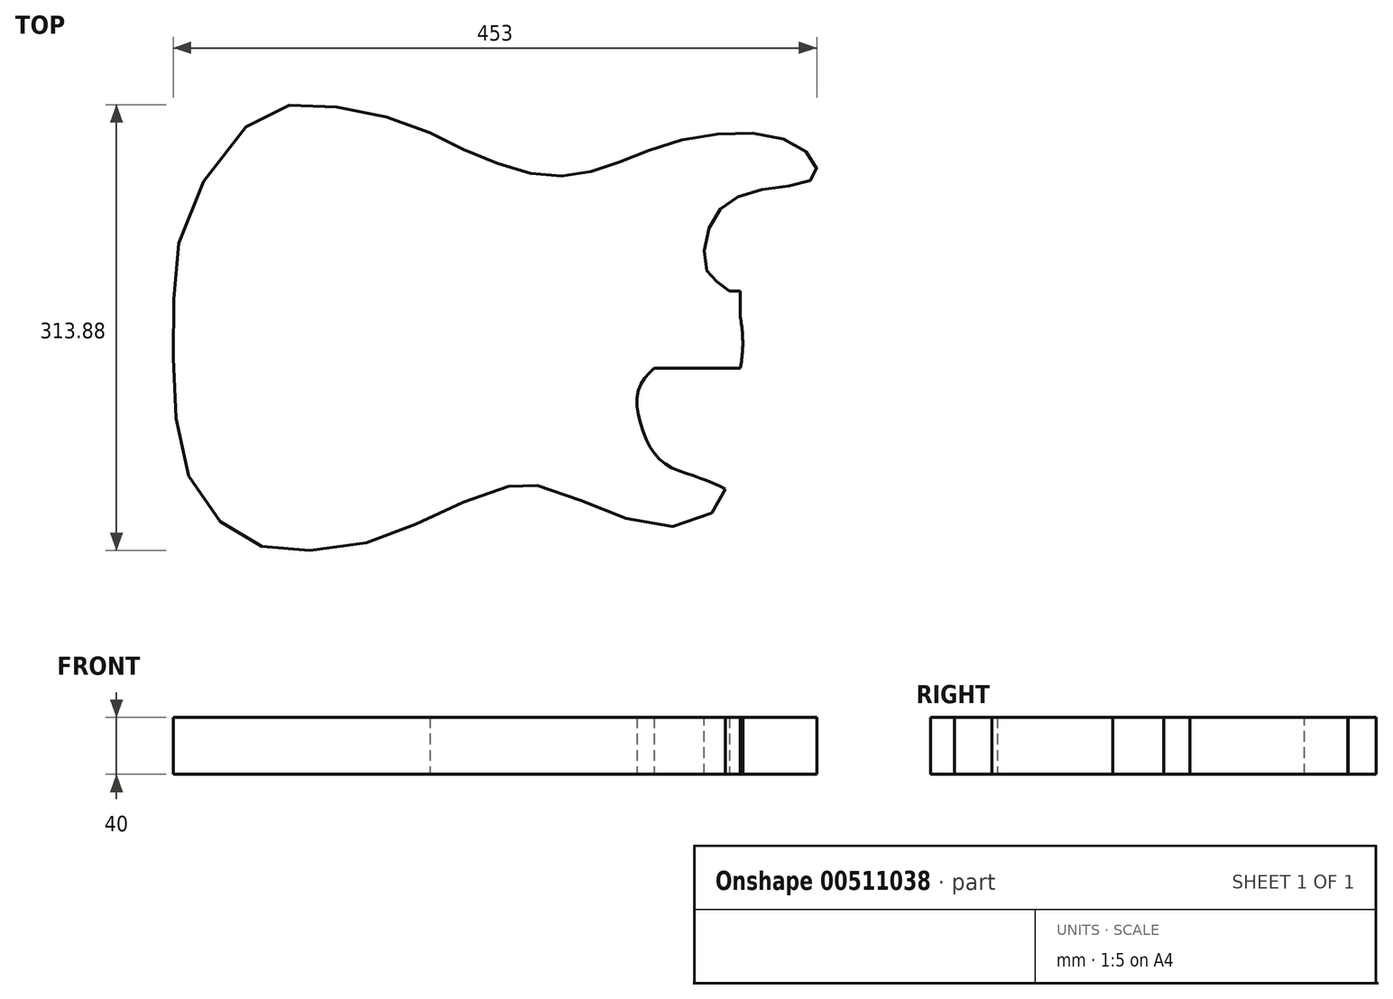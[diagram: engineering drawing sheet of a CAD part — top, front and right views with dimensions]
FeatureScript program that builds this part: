
annotation { "Feature Type Name" : "Feature", "Feature Type Description" : "" }
export const myFeature = defineFeature(function(context is Context, id is Id, definition is map)
    precondition{}
    {
        {
            var Q0;
            Q0=qCreatedBy(makeId("Top.planeOp"),FACE);
            var sketch = newSketch(context, id + "F0", { "sketchPlane" : qUnion([Q0])});
            skFitSpline(sketch, "E0", {"points": [v(186.62, 300.1) * mm, v(280.66, 269.49) * mm, v(356.08, 292.85) * mm, v(444.56, 291.8) * mm, v(457.87, 269.36) * mm, v(415.59, 259.08) * mm, v(384.5, 236.24) * mm, v(382.85, 200.63) * mm, v(397.5, 188.64) * mm, v(405.1, 134.41) * mm], "startDerivative": vector(611.69, -318.98) * mm, "endDerivative": vector(-113.06, -510.75) * mm});
            skFitSpline(sketch, "E1", {"points": [v(186.62, 300.1) * mm, v(148.03, 313.33) * mm, v(101.02, 319.83) * mm, v(64.85, 310.43) * mm, v(15.66, 241.74) * mm, v(6.26, 180.28) * mm, v(6.98, 114.48) * mm, v(20, 51.57) * mm, v(56.17, 13.97) * mm, v(95.23, 6.02) * mm, v(153.1, 14.7) * mm, v(197.94, 34.94) * mm, v(241.35, 50.85) * mm, v(255.09, 53.02) * mm, v(286.92, 43.62) * mm, v(328.15, 27.7) * mm, v(367.2, 24.1) * mm, v(390.35, 37.83) * mm, v(394.7, 49.4) * mm], "startDerivative": vector(-683.32, 269.89) * mm, "endDerivative": vector(74.42, 390) * mm});
            skFitSpline(sketch, "E2", {"points": [v(394.7, 49.4) * mm, v(375.89, 57.36) * mm, v(352.74, 66.76) * mm, v(337.55, 87.73) * mm, v(333.2, 118.1) * mm, v(344.78, 134.73) * mm], "startDerivative": vector(-97.43, 45.56) * mm, "endDerivative": vector(80.57, 79.08) * mm});
            skFitSpline(sketch, "E3", {"points": [v(344.78, 134.73) * mm, v(370.82, 134.73) * mm, v(371.55, 134.73) * mm], "startDerivative": vector(41.23, 0) * mm, "endDerivative": vector(3.26, 0) * mm});
            skLineSegment(sketch, "E4.bottom", {"start": v(328.54, 188.64) * mm, "end": v(405.1, 188.64) * mm});
            skLineSegment(sketch, "E4.top", {"start": v(328.54, 134.41) * mm, "end": v(405.1, 134.41) * mm});
            skLineSegment(sketch, "E4.left", {"start": v(328.54, 188.64) * mm, "end": v(328.54, 134.41) * mm});
            skLineSegment(sketch, "E4.right", {"start": v(405.1, 188.64) * mm, "end": v(405.1, 134.41) * mm});
            skPoint(sketch, "E5", {"position": v(389.37, 194.94) * mm});
            skPoint(sketch, "E6", {"position": v(405.1, 170.45) * mm});
            skSolve(sketch);
        }
        {
            var Q0;
            Q0 = qSketchRegion(id + "F0", true);
            extrude(context, id + "F1", {"entities" : qUnion([Q0]), "depth" : 40 * mm});
        }
    });
